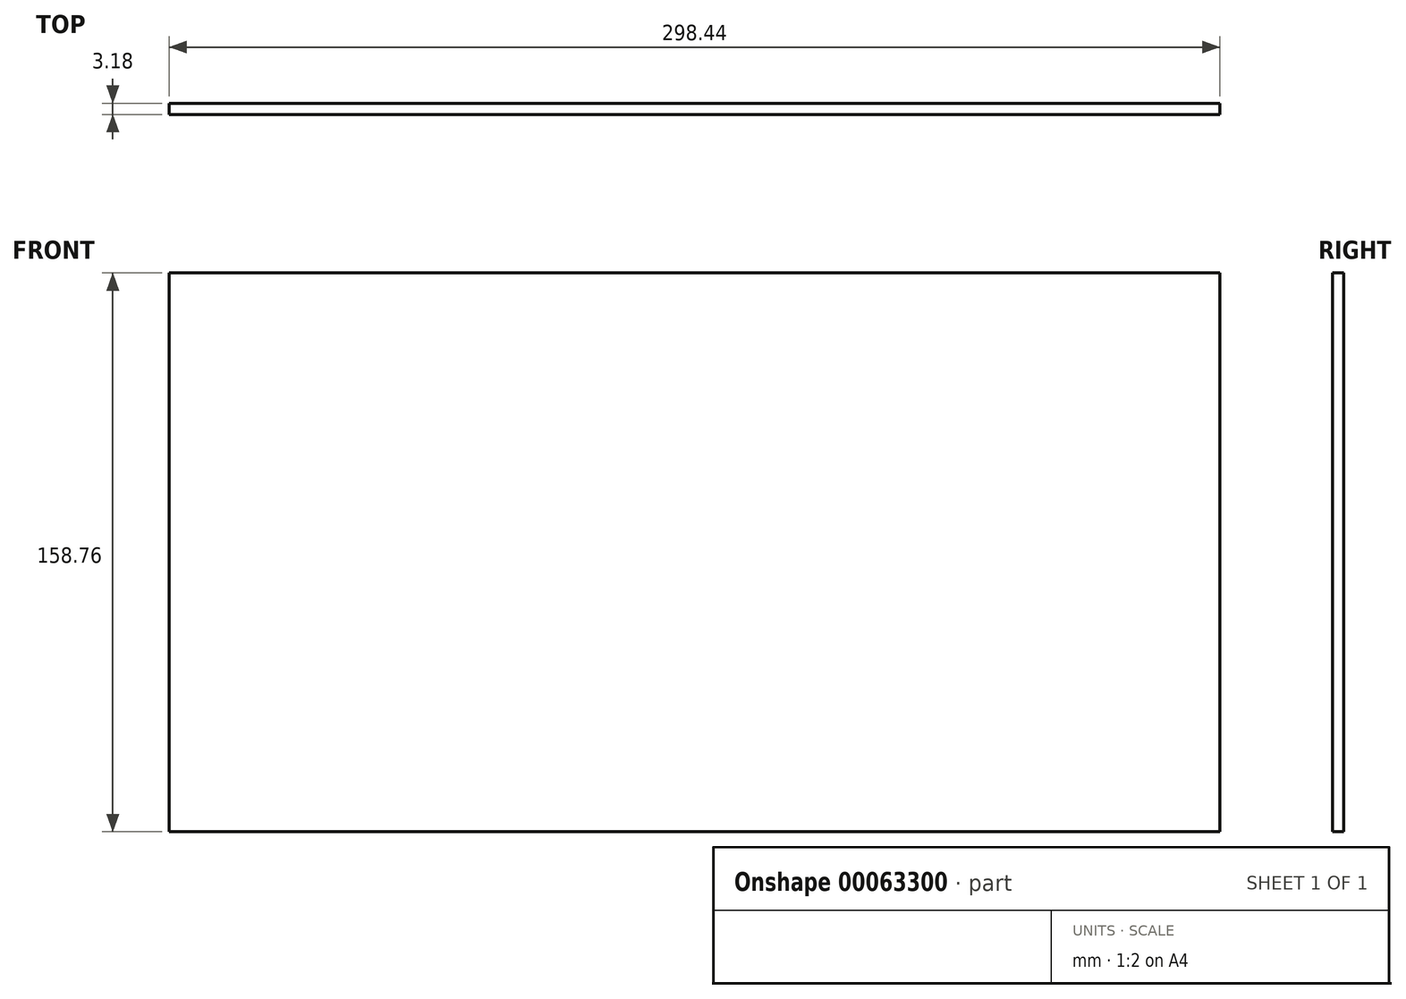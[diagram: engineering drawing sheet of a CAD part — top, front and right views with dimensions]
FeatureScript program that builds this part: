
annotation { "Feature Type Name" : "Feature", "Feature Type Description" : "" }
export const myFeature = defineFeature(function(context is Context, id is Id, definition is map)
    precondition{}
    {
        {
            var Q0;
            Q0=qCreatedBy(makeId("Front.planeOp"),FACE);
            var sketch = newSketch(context, id + "F0", { "sketchPlane" : qUnion([Q0])});
            skLineSegment(sketch, "E0.rect.bottom", {"start": v(149.23, 79.38) * mm, "end": v(-149.23, 79.38) * mm});
            skLineSegment(sketch, "E0.rect.top", {"start": v(149.23, -79.38) * mm, "end": v(-149.23, -79.38) * mm});
            skLineSegment(sketch, "E0.rect.left", {"start": v(149.23, 79.38) * mm, "end": v(149.23, -79.38) * mm});
            skLineSegment(sketch, "E0.rect.right", {"start": v(-149.23, 79.38) * mm, "end": v(-149.23, -79.38) * mm});
            skPoint(sketch, "E0.rect.middle", {"position": v(0, 0) * mm});
            skSolve(sketch);
        }
        {
            var Q0;
            Q0=makeQuery(id+"F0.imprint","IMPRINT",FACE,{"disambiguationData":[TD([[makeQuery(id+"F0.imprint","IMPRINT",EDGE,{"derivedFrom":sQuery(id+"F0.wireOp",EDGE,"E0.rect.bottom")}),1.0]])]});
            extrude(context, id + "F1", {"entities" : qUnion([Q0]), "depth" : 3.17 * mm, "symmetric" : true});
        }
    });
